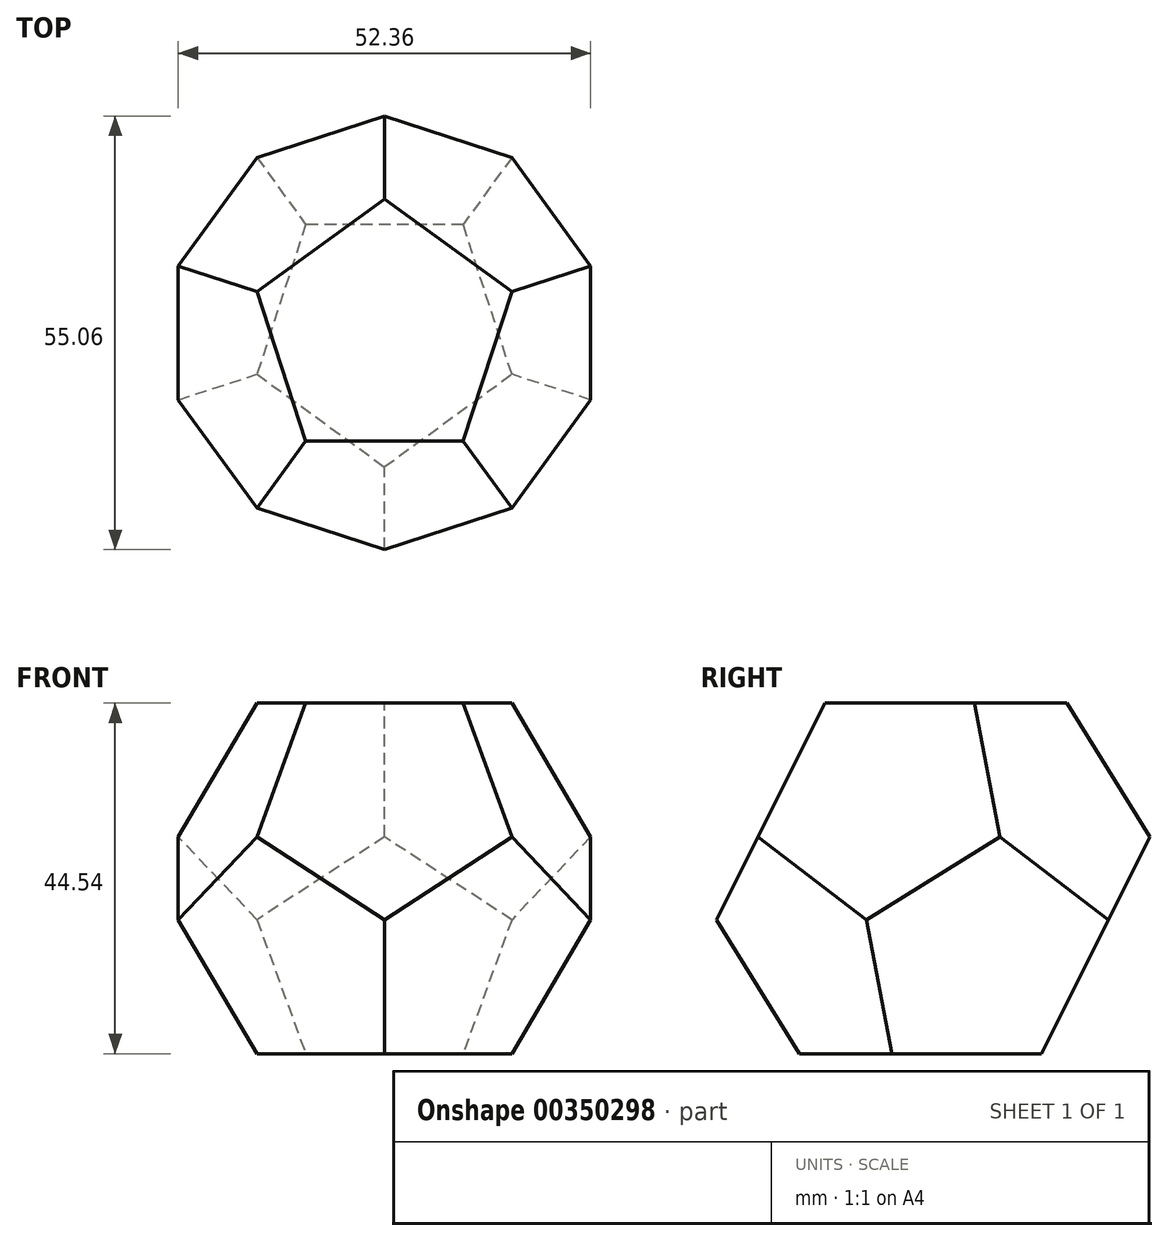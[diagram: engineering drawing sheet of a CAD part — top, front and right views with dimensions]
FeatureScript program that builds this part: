
annotation { "Feature Type Name" : "Feature", "Feature Type Description" : "" }
export const myFeature = defineFeature(function(context is Context, id is Id, definition is map)
    precondition{}
    {
        {
            var Q0;
            Q0=qCreatedBy(makeId("Top.planeOp"),FACE);
            var sketch = newSketch(context, id + "F0", { "sketchPlane" : qUnion([Q0])});
            skLineSegment(sketch, "E0", {"start": v(-26.18, -36.03) * mm, "end": v(26.18, -36.03) * mm});
            skLineSegment(sketch, "E1", {"start": v(26.18, -36.03) * mm, "end": v(42.36, 13.76) * mm});
            skLineSegment(sketch, "E2", {"start": v(42.36, 13.76) * mm, "end": v(0, 44.54) * mm});
            skLineSegment(sketch, "E3", {"start": v(0, 44.54) * mm, "end": v(-42.36, 13.76) * mm});
            skLineSegment(sketch, "E4", {"start": v(-42.36, 13.76) * mm, "end": v(-26.18, -36.03) * mm});
            skLineSegment(sketch, "E5", {"start": v(0, 44.54) * mm, "end": v(26.18, -36.03) * mm, "construction": true});
            skLineSegment(sketch, "E6", {"start": v(42.36, 13.76) * mm, "end": v(-42.36, 13.76) * mm, "construction": true});
            skLineSegment(sketch, "E7", {"start": v(0, 44.54) * mm, "end": v(-26.18, -36.03) * mm, "construction": true});
            skPoint(sketch, "E8", {"position": v(-10, 13.76) * mm});
            skPoint(sketch, "E9", {"position": v(10, 13.76) * mm});
            skLineSegment(sketch, "E10", {"start": v(0, 0) * mm, "end": v(42.36, 13.76) * mm, "construction": true});
            skLineSegment(sketch, "E11", {"start": v(0, 0) * mm, "end": v(26.18, -36.03) * mm, "construction": true});
            skSolve(sketch);
        }
        {
            var Q0;
            Q0=qCreatedBy(makeId("Front.planeOp"),FACE);
            var sketch = newSketch(context, id + "F1", { "sketchPlane" : qUnion([Q0])});
            skLineSegment(sketch, "E12", {"start": v(0, -27.85) * mm, "end": v(0, -9.55) * mm, "construction": true});
            skSolve(sketch);
        }
        {
            var Q0;
            Q0=sQuery(id+"F1.wireOp",VERTEX,"E12.end");
            var Q1;
            Q1=sQuery(id+"F0.wireOp",VERTEX,"E10.start");
            var Q2;
            Q2=sQuery(id+"F0.wireOp",VERTEX,"E6.start");
            cPlane(context, id + "F2", {"entities" : qUnion([Q0, Q1, Q2]), "cplaneType" : CPlaneType.THREE_POINT, "offset" : 25 * mm, "width" : 150 * mm, "height" : 150 * mm});
        }
        {
            var Q0;
            Q0=qCreatedBy(id+"F2.planeOp",FACE);
            var sketch = newSketch(context, id + "F3", { "sketchPlane" : qUnion([Q0])});
            skPoint(sketch, "E13.0", {"position": v(44.54, 0) * mm});
            skLineSegment(sketch, "E14", {"start": v(44.54, 0) * mm, "end": v(0, 72.07) * mm, "construction": true});
            skSolve(sketch);
        }
        {
            var Q0;
            Q0=makeQuery(id+"F0.imprint","IMPRINT",FACE,{"disambiguationData":[TD([[makeQuery(id+"F0.imprint","IMPRINT",EDGE,{"derivedFrom":sQuery(id+"F0.wireOp",EDGE,"E0")}),1.0]])]});
            var Q1;
            Q1=sQuery(id+"F3.wireOp",VERTEX,"E14.end");
            loft(context, id + "F4", {"sheetProfilesArray" : [{ "sheetProfileEntities" : qUnion([Q0]) }, { "sheetProfileEntities" : qUnion([Q1]) }]});
        }
        {
            var Q0;
            Q0=makeQuery(id+"F4.opLoft","SWEPT_BODY",BODY,{"disambiguationData":[OSD([makeQuery(id+"F0.imprint","IMPRINT",FACE,{"disambiguationData":[TD([[makeQuery(id+"F0.imprint","IMPRINT",EDGE,{"derivedFrom":sQuery(id+"F0.wireOp",EDGE,"E0")}),1.0]])]}),sQuery(id+"F3.wireOp",VERTEX,"E14.end")])]});
            var Q1;
            Q1=sQuery(id+"FMufkRlIacc9sjD_0.wireOp",VERTEX,"HV1PuSsV-kqOY-zEMv-GmxQ-L67WcdgTZ8xZ.end");
            var Q2;
            Q2=sQuery(id+"FMufkRlIacc9sjD_0.wireOp",VERTEX,"GXqtPz0T-dAHT-fxn9-mHxR-smBkfAZc5GI9.end");
            var Q3;
            Q3=sQuery(id+"F1.wireOp",EDGE,"E12");
            transform(context, id + "F5", {"entities" : qUnion([Q0]), "transformType" : TransformType.TRANSLATION_DISTANCE, "transformDirection" : qUnion([Q3]), "distance" : 44.54 * mm, "makeCopy" : true});
        }
        {
            var Q0;
            Q0=makeQuery(id+"F5.opPattern","COPY",BODY,{"derivedFrom":makeQuery(id+"F4.opLoft","SWEPT_BODY",BODY,{"disambiguationData":[OSD([makeQuery(id+"F0.imprint","IMPRINT",FACE,{"disambiguationData":[TD([[makeQuery(id+"F0.imprint","IMPRINT",EDGE,{"derivedFrom":sQuery(id+"F0.wireOp",EDGE,"E0")}),1.0]])]}),sQuery(id+"F3.wireOp",VERTEX,"E14.end")])]}),"instanceName":"1"});
            var Q1;
            Q1=sQuery(id+"F1.wireOp",EDGE,"E12");
            transform(context, id + "F6", {"entities" : qUnion([Q0]), "transformType" : TransformType.ROTATION, "transformAxis" : qUnion([Q1]), "angle" : 180 * degree, "makeCopy" : false});
        }
        {
            var Q0;
            Q0=makeQuery(id+"F5.opPattern","COPY",BODY,{"derivedFrom":makeQuery(id+"F4.opLoft","SWEPT_BODY",BODY,{"disambiguationData":[OSD([makeQuery(id+"F0.imprint","IMPRINT",FACE,{"disambiguationData":[TD([[makeQuery(id+"F0.imprint","IMPRINT",EDGE,{"derivedFrom":sQuery(id+"F0.wireOp",EDGE,"E0")}),1.0]])]}),sQuery(id+"F3.wireOp",VERTEX,"E14.end")])]}),"instanceName":"1"});
            var Q1;
            Q1=makeQuery(id+"F5.opPattern","COPY",FACE,{"derivedFrom":makeQuery(id+"F4.opLoft","CAP_FACE",FACE,{"disambiguationData":[OSD([makeQuery(id+"F0.imprint","IMPRINT",FACE,{"disambiguationData":[TD([[makeQuery(id+"F0.imprint","IMPRINT",EDGE,{"derivedFrom":sQuery(id+"F0.wireOp",EDGE,"E0")}),1.0]])]})])],"isStart":true}),"instanceName":"1"});
            mirror(context, id + "F7", {"operationType" : NewBodyOperationType.INTERSECT, "entities" : qUnion([Q0]), "mirrorPlane" : qUnion([Q1])});
        }
    });
